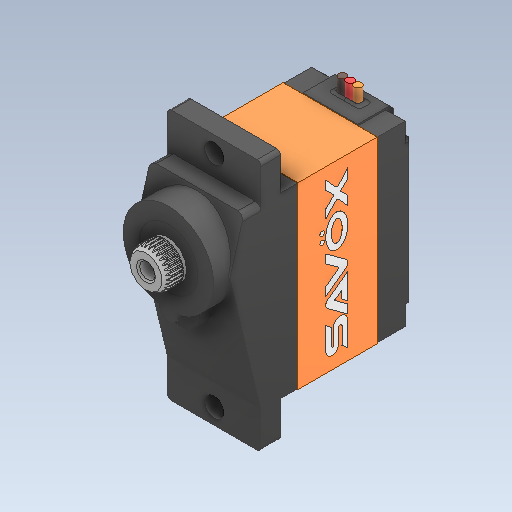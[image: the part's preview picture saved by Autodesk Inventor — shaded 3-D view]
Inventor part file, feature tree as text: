
AUTODESK INVENTOR PART (.ipt)
format: ipt  version: 2020.3 (Build 243373000, 373)  size: 913,920 bytes
history: native  units: mm
features: other x13, shell x1
ambient origin geometry x8: Origin, YZ Plane, XZ Plane, XY Plane, X Axis, Y Axis, Z Axis, Center Point
bodies: Solid1 (feature_tree), Solid2 (feature_tree), Solid3 (feature_tree), Solid4 (feature_tree), Solid5 (feature_tree), Solid6 (feature_tree), Solid7 (feature_tree), Solid8 (feature_tree), Solid9 (feature_tree), Solid10 (feature_tree), Solid11 (feature_tree), Solid12 (feature_tree), Solid13 (feature_tree), Solid14 (feature_tree)
feature tree (14):
  other  "brep_12"
  other  "brep_5"
  other  "brep_11"
  other  "brep_10"
  other  "brep_9"
  other  "brep_8"
  other  "brep_7"
  other  "brep_6"
  shell  "shell_1"  [1 undecoded]
  other  "brep_13"
  other  "brep_4"
  other  "brep_3"
  other  "brep_2"
  other  "brep_1"
note: 1 required parameter value undecoded (feature->parameter linkage not recoverable at this tier; creation-order binding heuristic only, values carry confidence <= 0.55)
